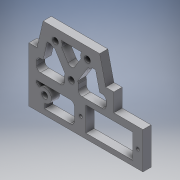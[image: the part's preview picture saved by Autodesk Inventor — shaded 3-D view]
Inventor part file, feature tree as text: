
AUTODESK INVENTOR PART (.ipt)
format: ipt  version: 2016 (Build 200138000, 138)  size: 235,008 bytes
history: native  units: in
note: dims shown in document units (in); Inventor stores cm internally (conversion verified against a paired STEP export)
features: extrude x6, sketch x6, fillet x3, direct_edit x1, move_body x1
ambient origin geometry x8: Origin, YZ Plane, XZ Plane, XY Plane, X Axis, Y Axis, Z Axis, Center Point
bodies: Solid1 (feature_tree)
feature tree (17):
  extrude  "Extrusion1"  Depth=0.1575in TaperAngle=0.0deg
  extrude  "Extrusion3"  Depth=0.3937in TaperAngle=0.0deg
  extrude  "Extrusion4"  Depth=0.3937in TaperAngle=0.0deg
  extrude  "Extrusion6"  Depth=0.374in
  extrude  "Extrusion7"  Depth=0.3937in TaperAngle=0.0deg
  extrude  "Extrusion8"  Depth=0.0787in
  fillet  "Fillet1"  Radius=0.8217in
  fillet  "Fillet2"  Radius=0.3937in
  fillet  "Fillet3"  Radius=0.2638in
  direct_edit  "Direct Edit2"
  sketch  "Sketch1"  dims[d4=0.063in d5=0.063in d14=0.1575in d15=0.0in]
  sketch  "Sketch3"  dims[d21=0.1181in d24=0.3937in d25=0.0in]
  sketch  "Sketch4"  dims[d29=0.1181in d32=0.3937in d33=0.0in]
  sketch  "Sketch6"  dims[d49=0.1181in d50=0.374in]
  sketch  "Sketch7"  dims[d51=0.3047in d52=0.3937in d53=0.0in]
  sketch  "Sketch8"  dims[d54=0.1181in d55=0.7169in d56=0.8217in d57=0.3937in d58=0.0in d59=0.2638in d60=0.2638in d61=0.2638in d65=0.2638in d66=0.0787in d67=0.0787in d68=0.3937in d69=0.0in d70=0.0787in d71=0.0787in d72=0.0787in d76=0.0in d77=0.0in d78=-0.0394in]
  move_body  "Move2"
